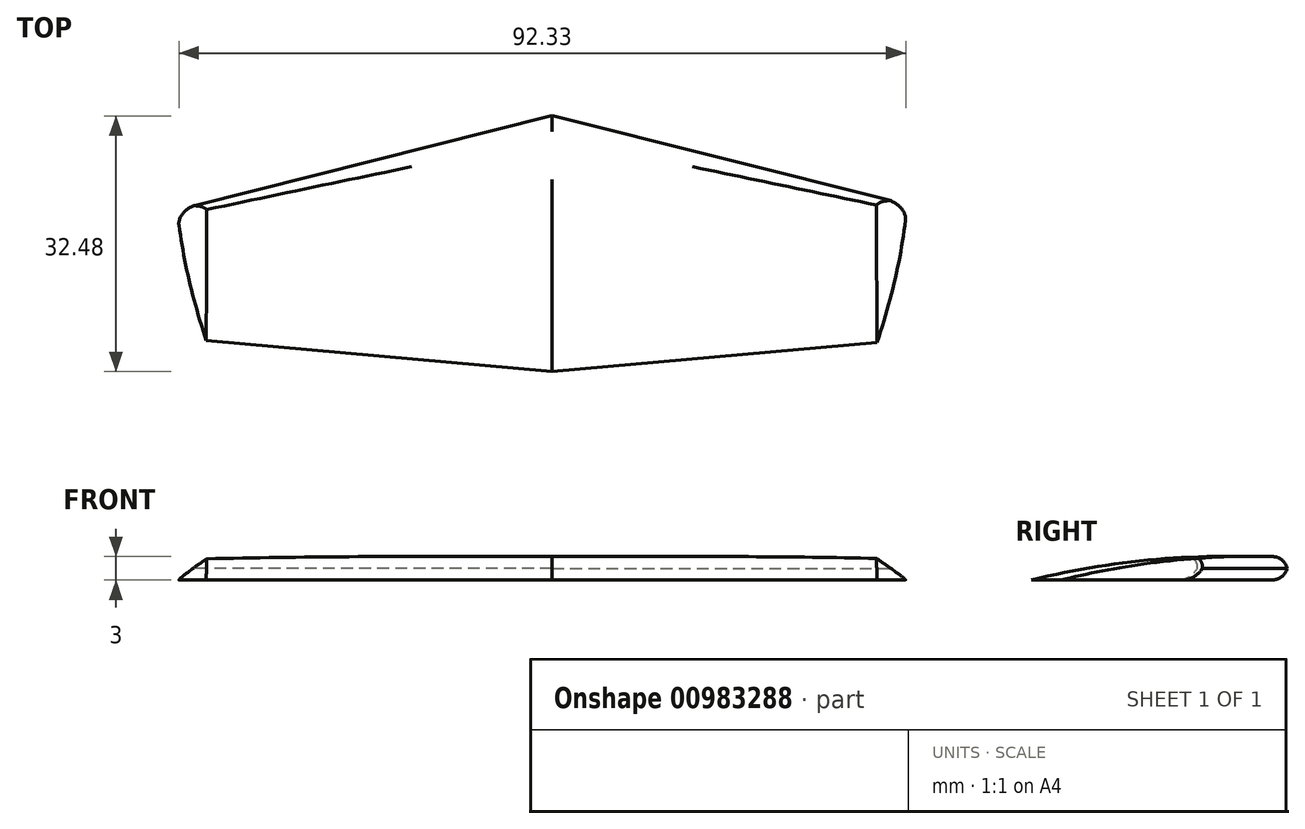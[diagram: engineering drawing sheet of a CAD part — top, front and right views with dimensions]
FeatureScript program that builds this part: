
annotation { "Feature Type Name" : "Feature", "Feature Type Description" : "" }
export const myFeature = defineFeature(function(context is Context, id is Id, definition is map)
    precondition{}
    {
        {
            var Q0;
            Q0=qCreatedBy(makeId("Top.planeOp"),FACE);
            var sketch = newSketch(context, id + "F0", { "sketchPlane" : qUnion([Q0])});
            skLineSegment(sketch, "E0", {"start": v(0, -21.14) * mm, "end": v(0, 14.89) * mm});
            skLineSegment(sketch, "E1", {"start": v(0, 14.89) * mm, "end": v(49.87, 2.38) * mm});
            skLineSegment(sketch, "E2", {"start": v(49.87, 2.38) * mm, "end": v(49.87, -16.67) * mm});
            skLineSegment(sketch, "E3", {"start": v(49.87, -16.67) * mm, "end": v(0, -21.14) * mm});
            skSolve(sketch);
        }
        {
            var Q0;
            Q0 = qSketchRegion(id + "F0", true);
            extrude(context, id + "F1", {"entities" : qUnion([Q0]), "depth" : 3 * mm, "offsetDistance" : 25 * mm});
        }
        {
            var Q0;
            Q0=makeQuery(id+"F1.opExtrude","CAP_EDGE",EDGE,{"disambiguationData":[OSD([sQuery(id+"F0.wireOp",EDGE,"E1")])],"isStart":false});
            var Q1;
            Q1=makeQuery(id+"F1.opExtrude","CAP_EDGE",EDGE,{"disambiguationData":[OSD([sQuery(id+"F0.wireOp",EDGE,"E1")])],"isStart":true});
            fillet(context, id + "F2", {"entities" : qUnion([Q0, Q1]), "radius" : 2 * mm, "tangentPropagation" : true, "allowEdgeOverflow" : false});
        }
        {
            var Q0;
            Q0=makeQuery(id+"F1.opExtrude","CAP_EDGE",EDGE,{"disambiguationData":[OSD([sQuery(id+"F0.wireOp",EDGE,"E3")])],"isStart":false});
            chamfer(context, id + "F3", {"entities" : qUnion([Q0]), "chamferType" : ChamferType.OFFSET_ANGLE, "width" : 5 * mm, "oppositeDirection" : false, "angle" : 60 * degree, "tangentPropagation" : true});
        }
        {
            var Q0;
            {var subQ0=sQuery(id+"F0.wireOp",EDGE,"E3");Q0=makeQuery(id+"F3.opChamfer","BLEND_EDGE",EDGE,{"blendedFrom":[makeQuery(id+"F1.opExtrude","CAP_EDGE",EDGE,{"disambiguationData":[OSD([subQ0])],"isStart":false}),makeQuery(id+"F1.opExtrude","CAP_FACE",FACE,{"disambiguationData":[OSD([sQuery(id+"F0.wireOp",EDGE,"E0"),sQuery(id+"F0.wireOp",EDGE,"E1"),sQuery(id+"F0.wireOp",EDGE,"E2"),subQ0])],"isStart":false})],"blendedInto":[makeQuery(id+"F1.opExtrude","CAP_FACE",FACE,{"disambiguationData":[OSD([sQuery(id+"F0.wireOp",EDGE,"E0"),sQuery(id+"F0.wireOp",EDGE,"E1"),sQuery(id+"F0.wireOp",EDGE,"E2"),subQ0])],"isStart":false})]});}
            fillet(context, id + "F4", {"entities" : qUnion([Q0]), "radius" : 100 * mm, "tangentPropagation" : true, "allowEdgeOverflow" : false});
        }
        {
            var Q0;
            Q0=makeQuery(id+"F1.opExtrude","SWEPT_BODY",BODY,{"disambiguationData":[OSD([sQuery(id+"F0.wireOp",EDGE,"E0"),sQuery(id+"F0.wireOp",EDGE,"E1"),sQuery(id+"F0.wireOp",EDGE,"E2"),sQuery(id+"F0.wireOp",EDGE,"E3")])]});
            var Q1;
            Q1=qCreatedBy(makeId("Right.planeOp"),FACE);
            mirror(context, id + "F5", {"operationType" : NewBodyOperationType.ADD, "entities" : qUnion([Q0]), "mirrorPlane" : qUnion([Q1])});
        }
        {
            var Q0;
            {var subQ0=sQuery(id+"F0.wireOp",EDGE,"E2");var subQ1=sQuery(id+"F0.wireOp",EDGE,"E3");Q0=makeQuery(id+"F4.opFillet","BLEND_EDGE",EDGE,{"blendedFrom":[makeQuery(id+"F3.opChamfer","BLEND_EDGE",EDGE,{"blendedFrom":[makeQuery(id+"F1.opExtrude","CAP_EDGE",EDGE,{"disambiguationData":[OSD([subQ1])],"isStart":false}),makeQuery(id+"F1.opExtrude","CAP_FACE",FACE,{"disambiguationData":[OSD([sQuery(id+"F0.wireOp",EDGE,"E0"),sQuery(id+"F0.wireOp",EDGE,"E1"),subQ0,subQ1])],"isStart":false})],"blendedInto":[makeQuery(id+"F1.opExtrude","CAP_FACE",FACE,{"disambiguationData":[OSD([sQuery(id+"F0.wireOp",EDGE,"E0"),sQuery(id+"F0.wireOp",EDGE,"E1"),subQ0,subQ1])],"isStart":false})]}),makeQuery(id+"F1.opExtrude","SWEPT_FACE",FACE,{"disambiguationData":[OSD([subQ0])]})],"blendedInto":[makeQuery(id+"F1.opExtrude","SWEPT_FACE",FACE,{"disambiguationData":[OSD([subQ0])]})]});}
            chamfer(context, id + "F6", {"entities" : qUnion([Q0]), "chamferType" : ChamferType.OFFSET_ANGLE, "width" : 6 * mm, "oppositeDirection" : false, "angle" : 55 * degree, "tangentPropagation" : true});
        }
        {
            var Q0;
            {var subQ0=sQuery(id+"F0.wireOp",EDGE,"E2");var subQ1=sQuery(id+"F0.wireOp",EDGE,"E3");Q0=makeQuery(id+"F5.opPattern","COPY",EDGE,{"derivedFrom":makeQuery(id+"F4.opFillet","BLEND_EDGE",EDGE,{"blendedFrom":[makeQuery(id+"F3.opChamfer","BLEND_EDGE",EDGE,{"blendedFrom":[makeQuery(id+"F1.opExtrude","CAP_EDGE",EDGE,{"disambiguationData":[OSD([subQ1])],"isStart":false}),makeQuery(id+"F1.opExtrude","CAP_FACE",FACE,{"disambiguationData":[OSD([sQuery(id+"F0.wireOp",EDGE,"E0"),sQuery(id+"F0.wireOp",EDGE,"E1"),subQ0,subQ1])],"isStart":false})],"blendedInto":[makeQuery(id+"F1.opExtrude","CAP_FACE",FACE,{"disambiguationData":[OSD([sQuery(id+"F0.wireOp",EDGE,"E0"),sQuery(id+"F0.wireOp",EDGE,"E1"),subQ0,subQ1])],"isStart":false})]}),makeQuery(id+"F1.opExtrude","SWEPT_FACE",FACE,{"disambiguationData":[OSD([subQ0])]})],"blendedInto":[makeQuery(id+"F1.opExtrude","SWEPT_FACE",FACE,{"disambiguationData":[OSD([subQ0])]})]}),"instanceName":"1"});}
            chamfer(context, id + "F7", {"entities" : qUnion([Q0]), "chamferType" : ChamferType.OFFSET_ANGLE, "width" : 6 * mm, "oppositeDirection" : false, "angle" : 35 * degree, "tangentPropagation" : true});
        }
    });
